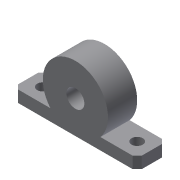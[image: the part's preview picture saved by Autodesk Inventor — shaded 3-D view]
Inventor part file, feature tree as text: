
AUTODESK INVENTOR PART (.ipt)
format: ipt  version: 2019.4 (Build 234330000, 330)  size: 131,072 bytes
history: native  units: mm
features: projected_geometry x3, extrude x2, sketch x2, chamfer x1
ambient origin geometry x8: Origin, YZ Plane, XZ Plane, XY Plane, X Axis, Y Axis, Z Axis, Center Point
bodies: Solid1 (feature_tree)
feature tree (8):
  extrude  "Extrusion1"  Depth=29.0mm
  extrude  "Extrusion2"  Depth=13.0mm
  chamfer  "Chamfer1"  Distance=5.19mm
  sketch  "Sketch1"  dims[d0=8.0mm d1=29.0mm]
  sketch  "Sketch2"  dims[d2=27.5mm d3=27.5mm d4=5.19mm d5=13.0mm d6=0.0mm d7=5.0mm d8=5.0mm d9=21.0mm d10=21.0mm d11=13.0mm d12=0.0mm d13=2.0mm d14=2.0mm d15=45.0deg]
  projected_geometry  "Projected Loop1"
  projected_geometry  "Projected Loop2"
  projected_geometry  "Projected Loop3"
